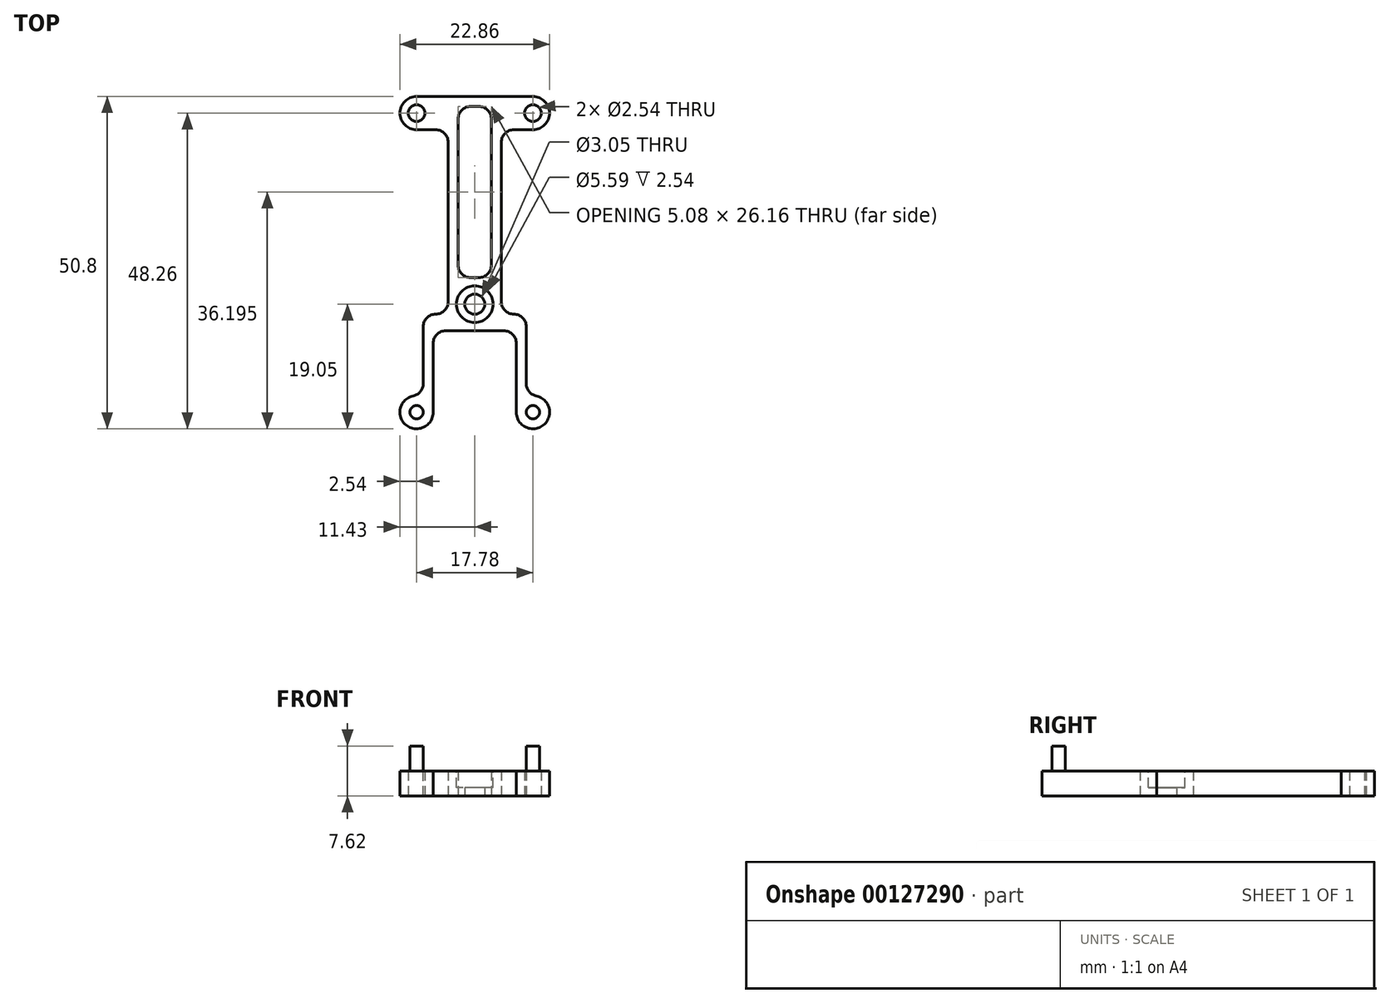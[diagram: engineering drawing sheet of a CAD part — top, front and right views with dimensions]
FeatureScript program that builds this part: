
annotation { "Feature Type Name" : "Feature", "Feature Type Description" : "" }
export const myFeature = defineFeature(function(context is Context, id is Id, definition is map)
    precondition{}
    {
        {
            var Q0;
            Q0=qCreatedBy(makeId("Top.planeOp"),FACE);
            var sketch = newSketch(context, id + "F0", { "sketchPlane" : qUnion([Q0])});
            skCircle(sketch, "E0", {"center": v(-8.9, 29.2) * mm, "radius": 1.27 * mm});
            skCircle(sketch, "E1", {"center": v(8.9, 29.2) * mm, "radius": 1.27 * mm});
            skCircle(sketch, "E2", {"center": v(-8.9, -16.51) * mm, "radius": 1 * mm, "construction": true});
            skCircle(sketch, "E3", {"center": v(8.89, -16.51) * mm, "radius": 1 * mm, "construction": true});
            skCircle(sketch, "E4", {"center": v(0, 0) * mm, "radius": 1.52 * mm});
            skLineSegment(sketch, "E5", {"start": v(-8.9, 29.2) * mm, "end": v(-8.9, 26.67) * mm, "construction": true});
            skLineSegment(sketch, "E6", {"start": v(8.89, -16.51) * mm, "end": v(6.35, -16.51) * mm, "construction": true});
            skLineSegment(sketch, "E7", {"start": v(-8.9, 29.2) * mm, "end": v(8.9, 29.2) * mm, "construction": true});
            skLineSegment(sketch, "E8", {"start": v(8.89, -16.51) * mm, "end": v(8.89, -13.97) * mm, "construction": true});
            skPoint(sketch, "E9", {"position": v(0, 29.2) * mm});
            skLineSegment(sketch, "E10", {"start": v(-8.89, 26.67) * mm, "end": v(-4.06, 26.67) * mm});
            skLineSegment(sketch, "E11", {"start": v(-4.06, 26.67) * mm, "end": v(-4.06, -1.52) * mm});
            skLineSegment(sketch, "E12", {"start": v(-4.06, -1.52) * mm, "end": v(-7.87, -1.52) * mm});
            skLineSegment(sketch, "E13", {"start": v(-7.87, -1.52) * mm, "end": v(-7.87, -13.97) * mm});
            skLineSegment(sketch, "E14", {"start": v(-7.87, -13.97) * mm, "end": v(-8.9, -13.97) * mm});
            skLineSegment(sketch, "E15", {"start": v(4.06, 26.67) * mm, "end": v(8.9, 26.67) * mm});
            skLineSegment(sketch, "E16", {"start": v(4.06, 26.67) * mm, "end": v(4.06, -1.52) * mm});
            skLineSegment(sketch, "E17", {"start": v(4.06, -1.52) * mm, "end": v(7.87, -1.52) * mm});
            skLineSegment(sketch, "E18", {"start": v(7.87, -1.52) * mm, "end": v(7.87, -13.97) * mm});
            skLineSegment(sketch, "E19", {"start": v(7.87, -13.97) * mm, "end": v(8.89, -13.97) * mm});
            skLineSegment(sketch, "E20", {"start": v(-6.35, -4.06) * mm, "end": v(6.35, -4.06) * mm});
            skLineSegment(sketch, "E21", {"start": v(6.35, -4.06) * mm, "end": v(6.35, -16.51) * mm});
            skPoint(sketch, "E22", {"position": v(0, -4.06) * mm});
            skLineSegment(sketch, "E23", {"start": v(-4.06, 26.67) * mm, "end": v(4.06, 26.67) * mm, "construction": true});
            skPoint(sketch, "E24", {"position": v(0, 26.67) * mm});
            skLineSegment(sketch, "E25", {"start": v(-6.35, -16.51) * mm, "end": v(-8.9, -16.51) * mm, "construction": true});
            skLineSegment(sketch, "E26", {"start": v(-8.9, -13.97) * mm, "end": v(-8.9, -16.51) * mm, "construction": true});
            skLineSegment(sketch, "E27", {"start": v(-6.35, -16.51) * mm, "end": v(-6.35, -4.06) * mm});
            skArc(sketch, "E28", {"start": v(-8.9, -13.97) * mm, "mid": v(-10.69, -18.3) * mm, "end": v(-6.35, -16.51) * mm});
            skArc(sketch, "E29", {"start": v(6.35, -16.51) * mm, "mid": v(10.69, -18.3) * mm, "end": v(8.89, -13.97) * mm});
            skLineSegment(sketch, "E30", {"start": v(6.35, -16.51) * mm, "end": v(-6.35, -16.51) * mm, "construction": true});
            skLineSegment(sketch, "E31", {"start": v(8.89, -13.97) * mm, "end": v(8.89, 29.2) * mm, "construction": true});
            skLineSegment(sketch, "E32", {"start": v(-6.35, -4.06) * mm, "end": v(-7.87, -4.06) * mm, "construction": true});
            skArc(sketch, "E33", {"start": v(-8.9, 31.75) * mm, "mid": v(-11.43, 29.2) * mm, "end": v(-8.89, 26.67) * mm});
            skArc(sketch, "E34", {"start": v(8.9, 26.67) * mm, "mid": v(11.43, 29.2) * mm, "end": v(8.9, 31.75) * mm});
            skLineSegment(sketch, "E35", {"start": v(-8.9, 26.67) * mm, "end": v(-8.9, -13.97) * mm, "construction": true});
            skLineSegment(sketch, "E36", {"start": v(-8.9, 31.75) * mm, "end": v(8.9, 31.75) * mm});
            skLineSegment(sketch, "E37", {"start": v(-4.06, 0) * mm, "end": v(-1.52, 0) * mm, "construction": true});
            skLineSegment(sketch, "E38", {"start": v(-6.35, -4.06) * mm, "end": v(-6.35, -1.52) * mm, "construction": true});
            skLineSegment(sketch, "E39.bottom", {"start": v(-2.54, 30.23) * mm, "end": v(2.54, 30.23) * mm});
            skLineSegment(sketch, "E39.top", {"start": v(-2.54, 4.06) * mm, "end": v(2.54, 4.06) * mm});
            skLineSegment(sketch, "E39.left", {"start": v(-2.54, 30.23) * mm, "end": v(-2.54, 4.06) * mm});
            skLineSegment(sketch, "E39.right", {"start": v(2.54, 30.23) * mm, "end": v(2.54, 4.06) * mm});
            skLineSegment(sketch, "E40", {"start": v(-2.54, 4.06) * mm, "end": v(-4.06, 4.06) * mm, "construction": true});
            skLineSegment(sketch, "E41", {"start": v(0, 1.52) * mm, "end": v(0, 4.06) * mm, "construction": true});
            skPoint(sketch, "E42", {"position": v(0, 30.23) * mm});
            skLineSegment(sketch, "E43", {"start": v(-2.54, 30.23) * mm, "end": v(-2.54, 31.75) * mm, "construction": true});
            skSolve(sketch);
        }
        {
            var Q0;
            Q0 = qSketchRegion(id + "F0", true);
            extrude(context, id + "F1", {"entities" : qUnion([Q0]), "depth" : 3.8 * mm});
        }
        {
            var Q0;
            Q0=makeQuery(id+"F1.opExtrude","SWEPT_EDGE",EDGE,{"disambiguationData":[OSD([sQuery(id+"F0.wireOp",EDGE,"E20"),sQuery(id+"F0.wireOp",EDGE,"E21")])]});
            var Q1;
            Q1=makeQuery(id+"F1.opExtrude","SWEPT_EDGE",EDGE,{"disambiguationData":[OSD([sQuery(id+"F0.wireOp",EDGE,"E20"),sQuery(id+"F0.wireOp",EDGE,"E27")])]});
            var Q2;
            Q2=makeQuery(id+"F1.opExtrude","SWEPT_EDGE",EDGE,{"disambiguationData":[OSD([sQuery(id+"F0.wireOp",EDGE,"E11"),sQuery(id+"F0.wireOp",EDGE,"E12")])]});
            var Q3;
            Q3=makeQuery(id+"F1.opExtrude","SWEPT_EDGE",EDGE,{"disambiguationData":[OSD([sQuery(id+"F0.wireOp",EDGE,"E12"),sQuery(id+"F0.wireOp",EDGE,"E13")])]});
            var Q4;
            Q4=makeQuery(id+"F1.opExtrude","SWEPT_EDGE",EDGE,{"disambiguationData":[OSD([sQuery(id+"F0.wireOp",EDGE,"E17"),sQuery(id+"F0.wireOp",EDGE,"E18")])]});
            var Q5;
            Q5=makeQuery(id+"F1.opExtrude","SWEPT_EDGE",EDGE,{"disambiguationData":[OSD([sQuery(id+"F0.wireOp",EDGE,"E15"),sQuery(id+"F0.wireOp",EDGE,"E16")])]});
            var Q6;
            Q6=makeQuery(id+"F1.opExtrude","SWEPT_EDGE",EDGE,{"disambiguationData":[OSD([sQuery(id+"F0.wireOp",EDGE,"E16"),sQuery(id+"F0.wireOp",EDGE,"E17")])]});
            var Q7;
            Q7=makeQuery(id+"F1.opExtrude","SWEPT_EDGE",EDGE,{"disambiguationData":[OSD([sQuery(id+"F0.wireOp",EDGE,"E10"),sQuery(id+"F0.wireOp",EDGE,"E11")])]});
            var Q8;
            Q8=makeQuery(id+"F1.opExtrude","SWEPT_EDGE",EDGE,{"disambiguationData":[OSD([sQuery(id+"F0.wireOp",EDGE,"E39.bottom"),sQuery(id+"F0.wireOp",EDGE,"E39.right")])]});
            var Q9;
            Q9=makeQuery(id+"F1.opExtrude","SWEPT_EDGE",EDGE,{"disambiguationData":[OSD([sQuery(id+"F0.wireOp",EDGE,"E39.bottom"),sQuery(id+"F0.wireOp",EDGE,"E39.left")])]});
            var Q10;
            Q10=makeQuery(id+"F1.opExtrude","SWEPT_EDGE",EDGE,{"disambiguationData":[OSD([sQuery(id+"F0.wireOp",EDGE,"E39.top"),sQuery(id+"F0.wireOp",EDGE,"E39.left")])]});
            var Q11;
            Q11=makeQuery(id+"F1.opExtrude","SWEPT_EDGE",EDGE,{"disambiguationData":[OSD([sQuery(id+"F0.wireOp",EDGE,"E39.top"),sQuery(id+"F0.wireOp",EDGE,"E39.right")])]});
            var Q12;
            Q12=makeQuery(id+"F1.opExtrude","SWEPT_EDGE",EDGE,{"disambiguationData":[OSD([sQuery(id+"F0.wireOp",EDGE,"E18"),sQuery(id+"F0.wireOp",EDGE,"E19")])]});
            var Q13;
            Q13=makeQuery(id+"F1.opExtrude","SWEPT_EDGE",EDGE,{"disambiguationData":[OSD([sQuery(id+"F0.wireOp",EDGE,"E13"),sQuery(id+"F0.wireOp",EDGE,"E14")])]});
            fillet(context, id + "F2", {"entities" : qUnion([Q0, Q1, Q2, Q3, Q4, Q5, Q6, Q7, Q8, Q9, Q10, Q11, Q12, Q13]), "radius" : 1.9 * mm, "tangentPropagation" : true, "allowEdgeOverflow" : false});
        }
        {
            var Q0;
            Q0=makeQuery(id+"F1.opExtrude","CAP_FACE",FACE,{"disambiguationData":[OSD([sQuery(id+"F0.wireOp",EDGE,"E0"),sQuery(id+"F0.wireOp",EDGE,"E1"),sQuery(id+"F0.wireOp",EDGE,"E4"),sQuery(id+"F0.wireOp",EDGE,"E10"),sQuery(id+"F0.wireOp",EDGE,"E11"),sQuery(id+"F0.wireOp",EDGE,"E12"),sQuery(id+"F0.wireOp",EDGE,"E13"),sQuery(id+"F0.wireOp",EDGE,"E14"),sQuery(id+"F0.wireOp",EDGE,"E15"),sQuery(id+"F0.wireOp",EDGE,"E16"),sQuery(id+"F0.wireOp",EDGE,"E17"),sQuery(id+"F0.wireOp",EDGE,"E18"),sQuery(id+"F0.wireOp",EDGE,"E19"),sQuery(id+"F0.wireOp",EDGE,"E20"),sQuery(id+"F0.wireOp",EDGE,"E21"),sQuery(id+"F0.wireOp",EDGE,"E27"),sQuery(id+"F0.wireOp",EDGE,"E28"),sQuery(id+"F0.wireOp",EDGE,"E29"),sQuery(id+"F0.wireOp",EDGE,"E33"),sQuery(id+"F0.wireOp",EDGE,"E34"),sQuery(id+"F0.wireOp",EDGE,"E36"),sQuery(id+"F0.wireOp",EDGE,"E39.bottom"),sQuery(id+"F0.wireOp",EDGE,"E39.top"),sQuery(id+"F0.wireOp",EDGE,"E39.left"),sQuery(id+"F0.wireOp",EDGE,"E39.right")])],"isStart":false});
            var sketch = newSketch(context, id + "F3", { "sketchPlane" : qUnion([Q0])});
            skCircle(sketch, "E44", {"center": v(-8.9, -16.51) * mm, "radius": 1.02 * mm});
            skCircle(sketch, "E45", {"center": v(8.9, -16.51) * mm, "radius": 1.02 * mm});
            skSolve(sketch);
        }
        {
            var Q0;
            Q0 = qSketchRegion(id + "F3", true);
            extrude(context, id + "F4", {"entities" : qUnion([Q0]), "operationType" : NewBodyOperationType.ADD, "depth" : 3.8 * mm});
        }
        {
            var Q0;
            Q0=makeQuery(id+"F1.opExtrude","CAP_FACE",FACE,{"disambiguationData":[OSD([sQuery(id+"F0.wireOp",EDGE,"E0"),sQuery(id+"F0.wireOp",EDGE,"E1"),sQuery(id+"F0.wireOp",EDGE,"E4"),sQuery(id+"F0.wireOp",EDGE,"E10"),sQuery(id+"F0.wireOp",EDGE,"E11"),sQuery(id+"F0.wireOp",EDGE,"E12"),sQuery(id+"F0.wireOp",EDGE,"E13"),sQuery(id+"F0.wireOp",EDGE,"E14"),sQuery(id+"F0.wireOp",EDGE,"E15"),sQuery(id+"F0.wireOp",EDGE,"E16"),sQuery(id+"F0.wireOp",EDGE,"E17"),sQuery(id+"F0.wireOp",EDGE,"E18"),sQuery(id+"F0.wireOp",EDGE,"E19"),sQuery(id+"F0.wireOp",EDGE,"E20"),sQuery(id+"F0.wireOp",EDGE,"E21"),sQuery(id+"F0.wireOp",EDGE,"E27"),sQuery(id+"F0.wireOp",EDGE,"E28"),sQuery(id+"F0.wireOp",EDGE,"E29"),sQuery(id+"F0.wireOp",EDGE,"E33"),sQuery(id+"F0.wireOp",EDGE,"E34"),sQuery(id+"F0.wireOp",EDGE,"E36"),sQuery(id+"F0.wireOp",EDGE,"E39.bottom"),sQuery(id+"F0.wireOp",EDGE,"E39.top"),sQuery(id+"F0.wireOp",EDGE,"E39.left"),sQuery(id+"F0.wireOp",EDGE,"E39.right")])],"isStart":false});
            var sketch = newSketch(context, id + "F5", { "sketchPlane" : qUnion([Q0])});
            skCircle(sketch, "E46", {"center": v(0, 0) * mm, "radius": 2.8 * mm});
            skSolve(sketch);
        }
        {
            var Q0;
            Q0 = qSketchRegion(id + "F5", true);
            extrude(context, id + "F6", {"entities" : qUnion([Q0]), "operationType" : NewBodyOperationType.REMOVE, "oppositeDirection" : true, "depth" : 2.54 * mm});
        }
    });
